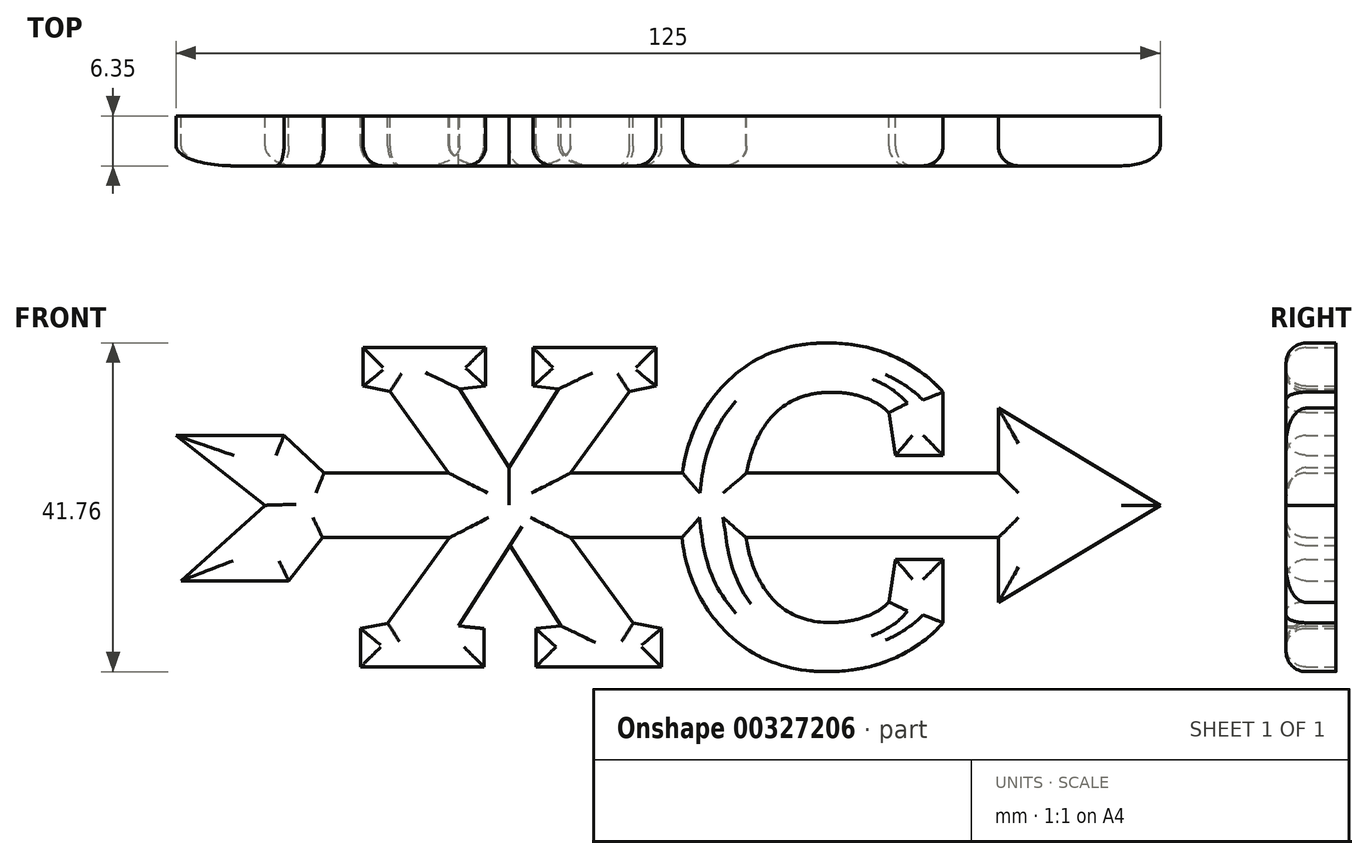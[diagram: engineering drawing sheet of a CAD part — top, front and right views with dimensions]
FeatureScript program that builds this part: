
annotation { "Feature Type Name" : "Feature", "Feature Type Description" : "" }
export const myFeature = defineFeature(function(context is Context, id is Id, definition is map)
    precondition{}
    {
        {
            var Q0;
            Q0=qCreatedBy(makeId("Front.planeOp"),FACE);
            var sketch = newSketch(context, id + "F0", { "sketchPlane" : qUnion([Q0])});
            skText(sketch, "E0", { "text": "XC", "fontName": "RobotoSlab-Bold.ttf"});
            skLineSegment(sketch, "E1", {"start": v(47.4, 20.28) * mm, "end": v(-45.76, 20.28) * mm});
            skLineSegment(sketch, "E2", {"start": v(-45.76, 20.28) * mm, "end": v(-45.76, 12.06) * mm});
            skLineSegment(sketch, "E3", {"start": v(-45.76, 12.06) * mm, "end": v(47.4, 12.06) * mm});
            skLineSegment(sketch, "E4", {"start": v(47.4, 12.06) * mm, "end": v(47.4, 20.28) * mm});
            skLineSegment(sketch, "E5", {"start": v(47.4, 20.28) * mm, "end": v(47.4, 28.5) * mm});
            skLineSegment(sketch, "E6", {"start": v(47.4, 28.5) * mm, "end": v(67.95, 16.17) * mm});
            skLineSegment(sketch, "E7", {"start": v(67.95, 16.17) * mm, "end": v(47.4, 3.84) * mm});
            skLineSegment(sketch, "E8", {"start": v(47.4, 3.84) * mm, "end": v(47.4, 12.06) * mm});
            skLineSegment(sketch, "E9", {"start": v(-45.76, 16.17) * mm, "end": v(-57.05, 25.04) * mm});
            skLineSegment(sketch, "E10", {"start": v(-57.05, 25.04) * mm, "end": v(-43.35, 25.04) * mm});
            skLineSegment(sketch, "E11", {"start": v(-43.35, 25.04) * mm, "end": v(-38.26, 20.28) * mm});
            skLineSegment(sketch, "E12", {"start": v(-45.76, 16.17) * mm, "end": v(-56.45, 6.58) * mm});
            skLineSegment(sketch, "E13", {"start": v(-56.45, 6.58) * mm, "end": v(-42.75, 6.58) * mm});
            skLineSegment(sketch, "E14", {"start": v(-42.75, 6.58) * mm, "end": v(-38.44, 12.06) * mm});
            const initialGuessF0  = {"E0": [-0.03452, -0.00438, 1, 0, 0.0411]};
            skSetInitialGuess(sketch, initialGuessF0);
            skSolve(sketch);
        }
        {
            var Q0;
            Q0 = qSketchRegion(id + "F0", true);
            extrude(context, id + "F1", {"entities" : qUnion([Q0]), "depth" : 6.35 * mm});
        }
        {
            var Q0;
            Q0=makeQuery(id+"F1.opExtrude","CAP_EDGE",EDGE,{"disambiguationData":[OSD([sQuery(id+"F0.wireOp",EDGE,"E10")])],"isStart":false});
            var Q1;
            {var subQ0=sQuery(id+"F0.wireOp",EDGE,"E1");Q1=makeQuery(id+"F1.opExtrude","CAP_EDGE",EDGE,{"disambiguationData":[OSD([subQ0]),TDD([makeQuery(id+"F0.imprint","IMPRINT",EDGE,{"disambiguationData":[TD([[makeQuery(id+"F0.imprint","INTERSECT",VERTEX,{"derivedFrom":[subQ0,sQuery(id+"F0.wireOp",EDGE,"E11")]}),1.0]])],"derivedFrom":subQ0})])],"isStart":false});}
            var Q2;
            Q2=makeQuery(id+"F1.opExtrude","CAP_EDGE",EDGE,{"disambiguationData":[OSD([sQuery(id+"F0.wireOp",EDGE,"E11")])],"isStart":false});
            var Q3;
            Q3=makeQuery(id+"F1.opExtrude","CAP_EDGE",EDGE,{"disambiguationData":[OSD([sQuery(id+"F0.wireOp",EDGE,"E9")])],"isStart":false});
            var Q4;
            Q4=makeQuery(id+"F1.opExtrude","CAP_EDGE",EDGE,{"disambiguationData":[OSD([sQuery(id+"F0.wireOp",EDGE,"E12")])],"isStart":false});
            var Q5;
            Q5=makeQuery(id+"F1.opExtrude","CAP_EDGE",EDGE,{"disambiguationData":[OSD([sQuery(id+"F0.wireOp",EDGE,"E13")])],"isStart":false});
            var Q6;
            Q6=makeQuery(id+"F1.opExtrude","CAP_EDGE",EDGE,{"disambiguationData":[OSD([sQuery(id+"F0.wireOp",EDGE,"E14")])],"isStart":false});
            var Q7;
            {var subQ0=sQuery(id+"F0.wireOp",EDGE,"E3");Q7=makeQuery(id+"F1.opExtrude","CAP_EDGE",EDGE,{"disambiguationData":[OSD([subQ0]),TDD([makeQuery(id+"F0.imprint","IMPRINT",EDGE,{"disambiguationData":[TD([[makeQuery(id+"F0.imprint","INTERSECT",VERTEX,{"derivedFrom":[subQ0,sQuery(id+"F0.wireOp",EDGE,"E14")]}),-1.0]])],"derivedFrom":subQ0})])],"isStart":false});}
            var Q8;
            Q8=makeQuery(id+"F1.opExtrude","CAP_EDGE",EDGE,{"disambiguationData":[OSD([sQuery(id+"F0.wireOp",EDGE,"E0.sketch_text.stroke-1")])],"isStart":false});
            var Q9;
            Q9=makeQuery(id+"F1.opExtrude","CAP_EDGE",EDGE,{"disambiguationData":[OSD([sQuery(id+"F0.wireOp",EDGE,"E0.sketch_text.stroke-0")])],"isStart":false});
            var Q10;
            Q10=makeQuery(id+"F1.opExtrude","CAP_EDGE",EDGE,{"disambiguationData":[OSD([sQuery(id+"F0.wireOp",EDGE,"E0.sketch_text.stroke-27")])],"isStart":false});
            var Q11;
            Q11=makeQuery(id+"F1.opExtrude","CAP_EDGE",EDGE,{"disambiguationData":[OSD([sQuery(id+"F0.wireOp",EDGE,"E0.sketch_text.stroke-26")])],"isStart":false});
            var Q12;
            Q12=makeQuery(id+"F1.opExtrude","CAP_EDGE",EDGE,{"disambiguationData":[OSD([sQuery(id+"F0.wireOp",EDGE,"E0.sketch_text.stroke-25")])],"isStart":false});
            var Q13;
            Q13=makeQuery(id+"F1.opExtrude","CAP_EDGE",EDGE,{"disambiguationData":[OSD([sQuery(id+"F0.wireOp",EDGE,"E0.sketch_text.stroke-2")])],"isStart":false});
            var Q14;
            Q14=makeQuery(id+"F1.opExtrude","CAP_EDGE",EDGE,{"disambiguationData":[OSD([sQuery(id+"F0.wireOp",EDGE,"E0.sketch_text.stroke-4")])],"isStart":false});
            var Q15;
            Q15=makeQuery(id+"F1.opExtrude","CAP_EDGE",EDGE,{"disambiguationData":[OSD([sQuery(id+"F0.wireOp",EDGE,"E0.sketch_text.stroke-6")])],"isStart":false});
            var Q16;
            Q16=makeQuery(id+"F1.opExtrude","CAP_EDGE",EDGE,{"disambiguationData":[OSD([sQuery(id+"F0.wireOp",EDGE,"E0.sketch_text.stroke-8")])],"isStart":false});
            var Q17;
            Q17=makeQuery(id+"F1.opExtrude","CAP_EDGE",EDGE,{"disambiguationData":[OSD([sQuery(id+"F0.wireOp",EDGE,"E0.sketch_text.stroke-5")])],"isStart":false});
            var Q18;
            Q18=makeQuery(id+"F1.opExtrude","CAP_EDGE",EDGE,{"disambiguationData":[OSD([sQuery(id+"F0.wireOp",EDGE,"E0.sketch_text.stroke-9")])],"isStart":false});
            var Q19;
            Q19=makeQuery(id+"F1.opExtrude","CAP_EDGE",EDGE,{"disambiguationData":[OSD([sQuery(id+"F0.wireOp",EDGE,"E0.sketch_text.stroke-12")])],"isStart":false});
            var Q20;
            Q20=makeQuery(id+"F1.opExtrude","CAP_EDGE",EDGE,{"disambiguationData":[OSD([sQuery(id+"F0.wireOp",EDGE,"E0.sketch_text.stroke-13")])],"isStart":false});
            var Q21;
            Q21=makeQuery(id+"F1.opExtrude","CAP_EDGE",EDGE,{"disambiguationData":[OSD([sQuery(id+"F0.wireOp",EDGE,"E0.sketch_text.stroke-11")])],"isStart":false});
            var Q22;
            Q22=makeQuery(id+"F1.opExtrude","CAP_EDGE",EDGE,{"disambiguationData":[OSD([sQuery(id+"F0.wireOp",EDGE,"E0.sketch_text.stroke-15")])],"isStart":false});
            var Q23;
            {var subQ0=sQuery(id+"F0.wireOp",EDGE,"E1");Q23=makeQuery(id+"F1.opExtrude","CAP_EDGE",EDGE,{"disambiguationData":[OSD([subQ0]),TDD([makeQuery(id+"F0.imprint","IMPRINT",EDGE,{"disambiguationData":[TD([[makeQuery(id+"F0.imprint","INTERSECT",VERTEX,{"derivedFrom":[sQuery(id+"F0.wireOp",EDGE,"E0.sketch_text.stroke-15"),subQ0]}),1.0]])],"derivedFrom":subQ0})])],"isStart":false});}
            var Q24;
            Q24=makeQuery(id+"F1.opExtrude","CAP_EDGE",EDGE,{"disambiguationData":[OSD([sQuery(id+"F0.wireOp",EDGE,"E0.sketch_text.stroke-16")])],"isStart":false});
            var Q25;
            {var subQ0=sQuery(id+"F0.wireOp",EDGE,"E3");Q25=makeQuery(id+"F1.opExtrude","CAP_EDGE",EDGE,{"disambiguationData":[OSD([subQ0]),TDD([makeQuery(id+"F0.imprint","IMPRINT",EDGE,{"disambiguationData":[TD([[makeQuery(id+"F0.imprint","INTERSECT",VERTEX,{"derivedFrom":[sQuery(id+"F0.wireOp",EDGE,"E0.sketch_text.stroke-16"),subQ0]}),-1.0]])],"derivedFrom":subQ0})])],"isStart":false});}
            var Q26;
            Q26=makeQuery(id+"F1.opExtrude","CAP_EDGE",EDGE,{"disambiguationData":[OSD([sQuery(id+"F0.wireOp",EDGE,"E0.sketch_text.stroke-22")])],"isStart":false});
            var Q27;
            Q27=makeQuery(id+"F1.opExtrude","CAP_EDGE",EDGE,{"disambiguationData":[OSD([sQuery(id+"F0.wireOp",EDGE,"E0.sketch_text.stroke-19")])],"isStart":false});
            var Q28;
            Q28=makeQuery(id+"F1.opExtrude","CAP_EDGE",EDGE,{"disambiguationData":[OSD([sQuery(id+"F0.wireOp",EDGE,"E0.sketch_text.stroke-18")])],"isStart":false});
            var Q29;
            Q29=makeQuery(id+"F1.opExtrude","CAP_EDGE",EDGE,{"disambiguationData":[OSD([sQuery(id+"F0.wireOp",EDGE,"E0.sketch_text.stroke-21")])],"isStart":false});
            var Q30;
            Q30=makeQuery(id+"F1.opExtrude","CAP_EDGE",EDGE,{"disambiguationData":[OSD([sQuery(id+"F0.wireOp",EDGE,"E0.sketch_text.stroke-17")])],"isStart":false});
            var Q31;
            Q31=makeQuery(id+"F1.opExtrude","CAP_EDGE",EDGE,{"disambiguationData":[OSD([sQuery(id+"F0.wireOp",EDGE,"E0.sketch_text.stroke-20")])],"isStart":false});
            var Q32;
            Q32=makeQuery(id+"F1.opExtrude","CAP_EDGE",EDGE,{"disambiguationData":[OSD([sQuery(id+"F0.wireOp",EDGE,"E0.sketch_text.stroke-37")])],"isStart":false});
            var Q33;
            Q33=makeQuery(id+"F1.opExtrude","CAP_EDGE",EDGE,{"disambiguationData":[OSD([sQuery(id+"F0.wireOp",EDGE,"E0.sketch_text.stroke-39")])],"isStart":false});
            var Q34;
            Q34=makeQuery(id+"F1.opExtrude","CAP_EDGE",EDGE,{"disambiguationData":[OSD([sQuery(id+"F0.wireOp",EDGE,"E0.sketch_text.stroke-42")])],"isStart":false});
            var Q35;
            Q35=makeQuery(id+"F1.opExtrude","CAP_EDGE",EDGE,{"disambiguationData":[OSD([sQuery(id+"F0.wireOp",EDGE,"E0.sketch_text.stroke-40")])],"isStart":false});
            var Q36;
            Q36=makeQuery(id+"F1.opExtrude","CAP_EDGE",EDGE,{"disambiguationData":[OSD([sQuery(id+"F0.wireOp",EDGE,"E8")])],"isStart":false});
            var Q37;
            Q37=makeQuery(id+"F1.opExtrude","CAP_EDGE",EDGE,{"disambiguationData":[OSD([sQuery(id+"F0.wireOp",EDGE,"E0.sketch_text.stroke-41")])],"isStart":false});
            var Q38;
            Q38=makeQuery(id+"F1.opExtrude","CAP_EDGE",EDGE,{"disambiguationData":[OSD([sQuery(id+"F0.wireOp",EDGE,"E7")])],"isStart":false});
            var Q39;
            Q39=makeQuery(id+"F1.opExtrude","CAP_EDGE",EDGE,{"disambiguationData":[OSD([sQuery(id+"F0.wireOp",EDGE,"E6")])],"isStart":false});
            var Q40;
            Q40=makeQuery(id+"F1.opExtrude","CAP_EDGE",EDGE,{"disambiguationData":[OSD([sQuery(id+"F0.wireOp",EDGE,"E5")])],"isStart":false});
            var Q41;
            {var subQ0=sQuery(id+"F0.wireOp",EDGE,"E1");Q41=makeQuery(id+"F1.opExtrude","CAP_EDGE",EDGE,{"disambiguationData":[OSD([subQ0]),TDD([makeQuery(id+"F0.imprint","IMPRINT",EDGE,{"disambiguationData":[TD([[makeQuery(id+"F0.imprint","INTERSECT",VERTEX,{"derivedFrom":[sQuery(id+"F0.wireOp",EDGE,"E0.sketch_text.stroke-33"),subQ0]}),1.0]])],"derivedFrom":subQ0})])],"isStart":false});}
            var Q42;
            {var subQ0=sQuery(id+"F0.wireOp",EDGE,"E3");Q42=makeQuery(id+"F1.opExtrude","CAP_EDGE",EDGE,{"disambiguationData":[OSD([subQ0]),TDD([makeQuery(id+"F0.imprint","IMPRINT",EDGE,{"disambiguationData":[TD([[makeQuery(id+"F0.imprint","INTERSECT",VERTEX,{"derivedFrom":[sQuery(id+"F0.wireOp",EDGE,"E0.sketch_text.stroke-35"),subQ0]}),-1.0]])],"derivedFrom":subQ0})])],"isStart":false});}
            var Q43;
            Q43=makeQuery(id+"F1.opExtrude","CAP_EDGE",EDGE,{"disambiguationData":[OSD([sQuery(id+"F0.wireOp",EDGE,"E0.sketch_text.stroke-32")])],"isStart":false});
            var Q44;
            Q44=makeQuery(id+"F1.opExtrude","CAP_EDGE",EDGE,{"disambiguationData":[OSD([sQuery(id+"F0.wireOp",EDGE,"E0.sketch_text.stroke-29")])],"isStart":false});
            var Q45;
            Q45=makeQuery(id+"F1.opExtrude","CAP_EDGE",EDGE,{"disambiguationData":[OSD([sQuery(id+"F0.wireOp",EDGE,"E0.sketch_text.stroke-50")])],"isStart":false});
            var Q46;
            Q46=makeQuery(id+"F1.opExtrude","CAP_EDGE",EDGE,{"disambiguationData":[OSD([sQuery(id+"F0.wireOp",EDGE,"E0.sketch_text.stroke-28")])],"isStart":false});
            var Q47;
            Q47=makeQuery(id+"F1.opExtrude","CAP_EDGE",EDGE,{"disambiguationData":[OSD([sQuery(id+"F0.wireOp",EDGE,"E0.sketch_text.stroke-14")])],"isStart":false});
            var Q48;
            Q48=makeQuery(id+"F1.opExtrude","CAP_EDGE",EDGE,{"disambiguationData":[OSD([sQuery(id+"F0.wireOp",EDGE,"E0.sketch_text.stroke-10")])],"isStart":false});
            var Q49;
            Q49=makeQuery(id+"F1.opExtrude","CAP_EDGE",EDGE,{"disambiguationData":[OSD([sQuery(id+"F0.wireOp",EDGE,"E0.sketch_text.stroke-51")])],"isStart":false});
            var Q50;
            Q50=makeQuery(id+"F1.opExtrude","CAP_EDGE",EDGE,{"disambiguationData":[OSD([sQuery(id+"F0.wireOp",EDGE,"E0.sketch_text.stroke-7")])],"isStart":false});
            var Q51;
            Q51=makeQuery(id+"F1.opExtrude","CAP_EDGE",EDGE,{"disambiguationData":[OSD([sQuery(id+"F0.wireOp",EDGE,"E0.sketch_text.stroke-3")])],"isStart":false});
            fillet(context, id + "F2", {"entities" : qUnion([Q0, Q1, Q2, Q3, Q4, Q5, Q6, Q7, Q8, Q9, Q10, Q11, Q12, Q13, Q14, Q15, Q16, Q17, Q18, Q19, Q20, Q21, Q22, Q23, Q24, Q25, Q26, Q27, Q28, Q29, Q30, Q31, Q32, Q33, Q34, Q35, Q36, Q37, Q38, Q39, Q40, Q41, Q42, Q43, Q44, Q45, Q46, Q47, Q48, Q49, Q50, Q51]), "radius" : 2.54 * mm, "tangentPropagation" : true, "allowEdgeOverflow" : false});
        }
    });
